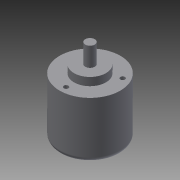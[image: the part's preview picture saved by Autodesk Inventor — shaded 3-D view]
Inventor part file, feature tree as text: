
AUTODESK INVENTOR PART (.ipt)
format: ipt  version: 2014 (Build 180170000, 170)  size: 122,368 bytes
history: native  units: mm
features: extrude x4, sketch x4, fillet x1
ambient origin geometry x8: Origin, YZ Plane, XZ Plane, XY Plane, X Axis, Y Axis, Z Axis, Center Point
bodies: Solid1 (feature_tree)
feature tree (9):
  extrude  "Extrusion1"  TaperAngle=120.0deg  [1 undecoded]
  extrude  "Extrusion2"  Depth=2.9mm
  fillet  "Fillet1"  Radius=6.0mm
  extrude  "Extrusion3"  Depth=15.0mm
  extrude  "Extrusion4"  Depth=10.0mm TaperAngle=0.0deg
  sketch  "Sketch1"  dims[d0=120.0deg d1=120.0deg]
  sketch  "Sketch2"  dims[d2=120.0deg d3=2.9mm d4=6.0mm]
  sketch  "Sketch3"  dims[d5=15.0mm d6=30.0mm]
  sketch  "Sketch4"  dims[d7=38.0mm d8=10.0mm d9=0.0mm d10=25.25mm d11=0.0mm d12=3.0mm d13=20.0mm d14=5.0mm d15=0.0mm d16=6.0mm d17=12.0mm d18=0.0mm]
note: 1 required parameter value undecoded (feature->parameter linkage not recoverable at this tier; creation-order binding heuristic only, values carry confidence <= 0.55)
